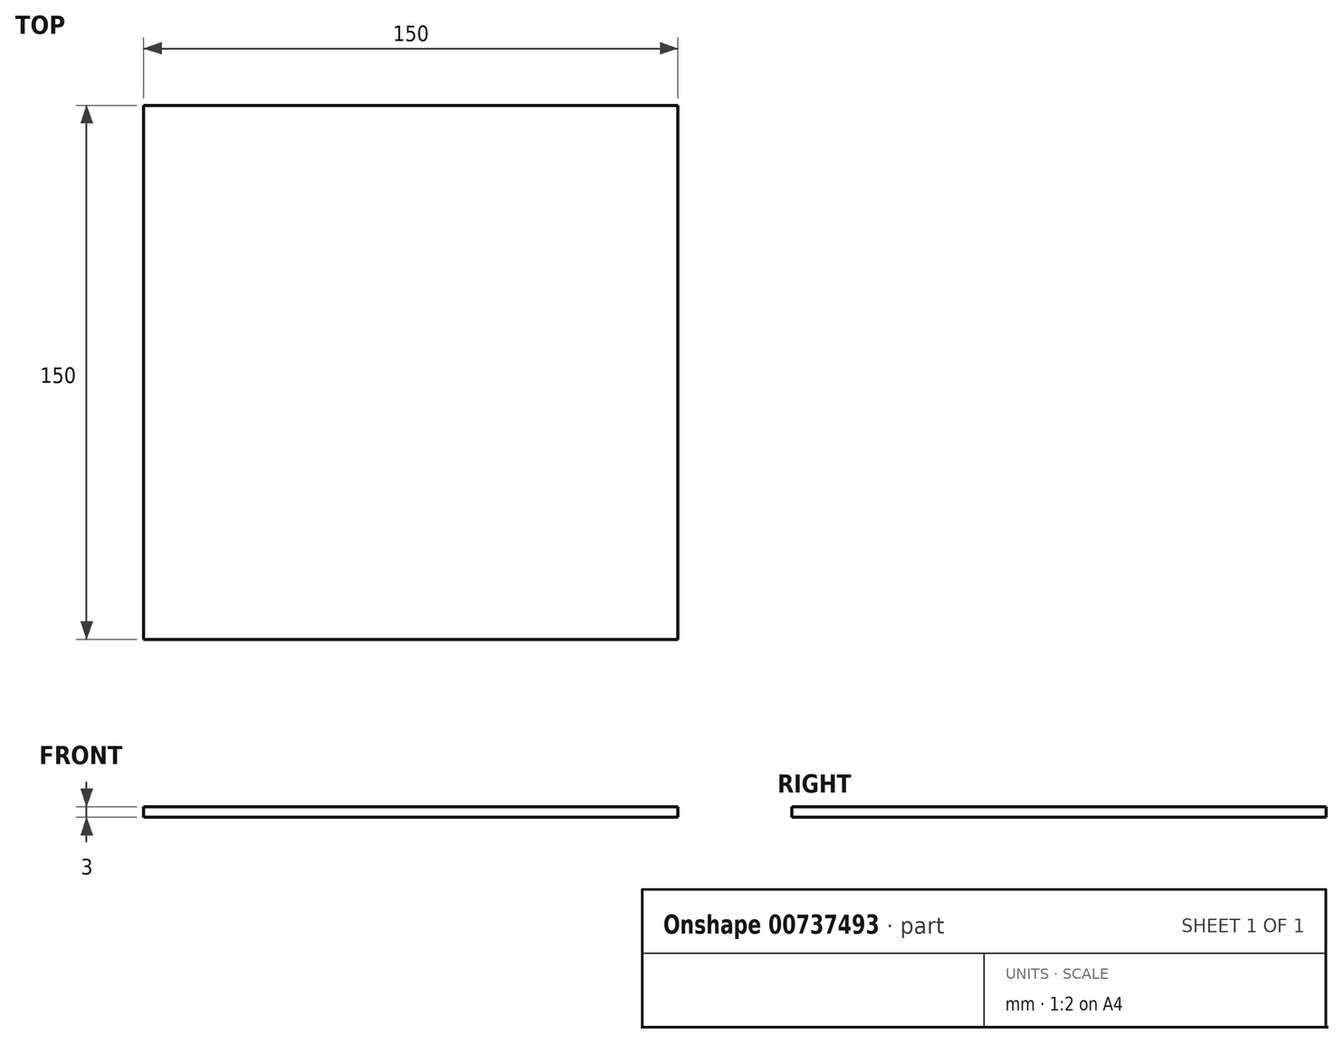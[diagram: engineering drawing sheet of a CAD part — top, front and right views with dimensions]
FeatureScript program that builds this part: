
annotation { "Feature Type Name" : "Feature", "Feature Type Description" : "" }
export const myFeature = defineFeature(function(context is Context, id is Id, definition is map)
    precondition{}
    {
        {
            var Q0;
            Q0=qCreatedBy(makeId("Top.planeOp"),FACE);
            var sketch = newSketch(context, id + "F0", { "sketchPlane" : qUnion([Q0])});
            skLineSegment(sketch, "E0.bottom", {"start": v(75, -75) * mm, "end": v(-75, -75) * mm});
            skLineSegment(sketch, "E0.top", {"start": v(75, 75) * mm, "end": v(-75, 75) * mm});
            skLineSegment(sketch, "E0.left", {"start": v(75, -75) * mm, "end": v(75, 75) * mm});
            skLineSegment(sketch, "E0.right", {"start": v(-75, -75) * mm, "end": v(-75, 75) * mm});
            skPoint(sketch, "E0.middle", {"position": v(0, 0) * mm});
            skSolve(sketch);
        }
        {
            var Q0;
            Q0=makeQuery(id+"F0.imprint","IMPRINT",FACE,{"disambiguationData":[TD([[makeQuery(id+"F0.imprint","IMPRINT",EDGE,{"derivedFrom":sQuery(id+"F0.wireOp",EDGE,"E0.bottom")}),-1.0]])]});
            extrude(context, id + "F1", {"entities" : qUnion([Q0]), "depth" : 3 * mm, "offsetDistance" : 25 * mm});
        }
    });
